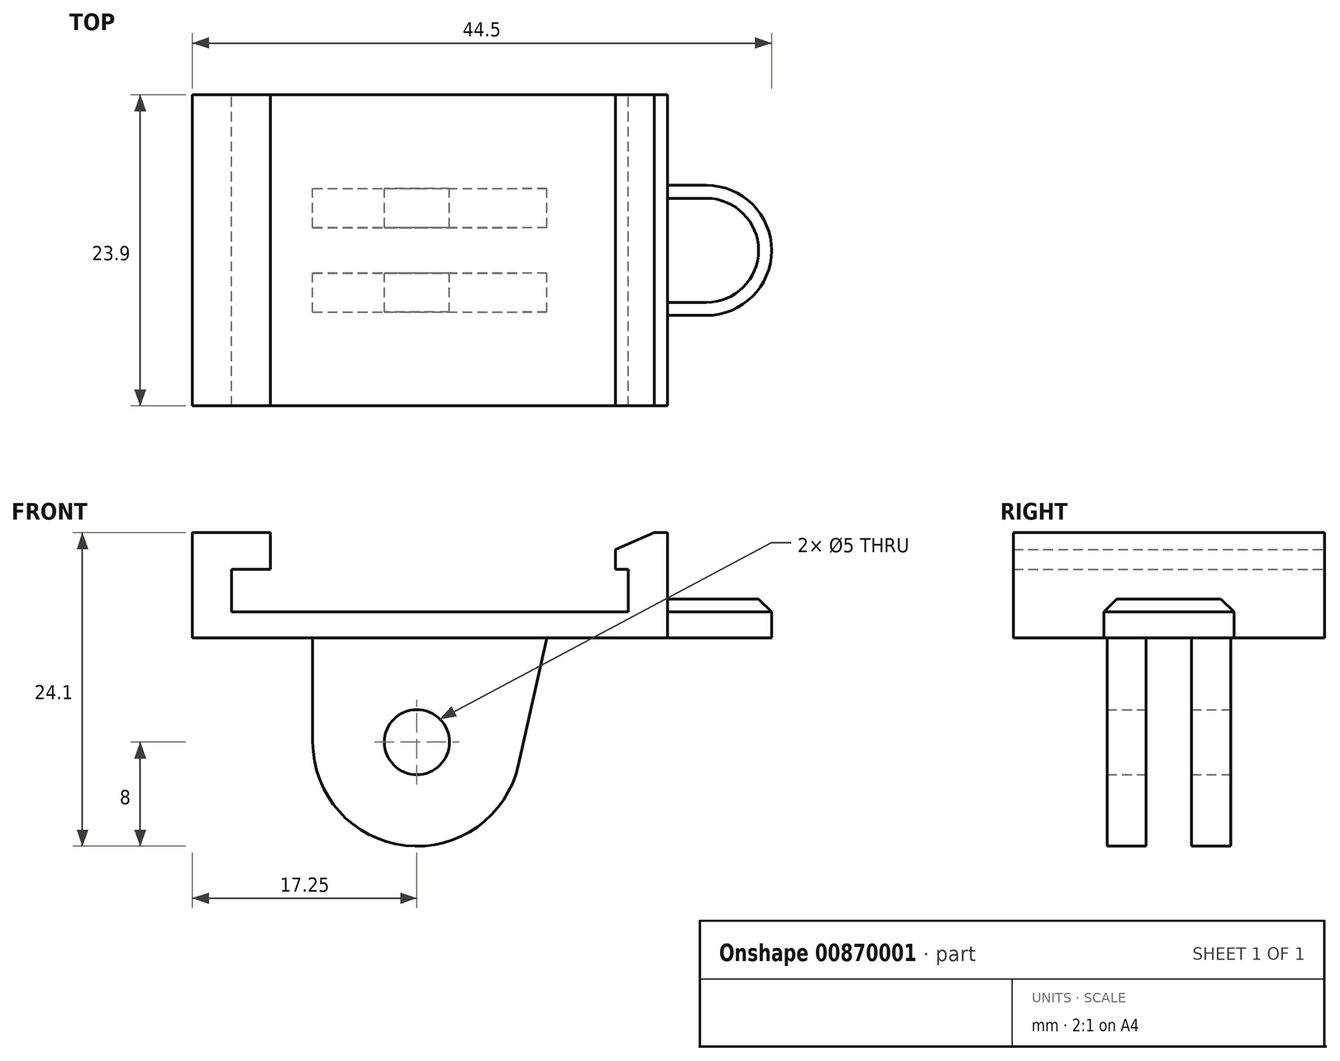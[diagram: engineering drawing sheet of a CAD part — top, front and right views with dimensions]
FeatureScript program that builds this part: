
annotation { "Feature Type Name" : "Feature", "Feature Type Description" : "" }
export const myFeature = defineFeature(function(context is Context, id is Id, definition is map)
    precondition{}
    {
        {
            var Q0;
            Q0=qCreatedBy(makeId("Front.planeOp"),FACE);
            var sketch = newSketch(context, id + "F0", { "sketchPlane" : qUnion([Q0])});
            skLineSegment(sketch, "E0", {"start": v(-12.25, 1.65) * mm, "end": v(-12.25, 4.45) * mm});
            skLineSegment(sketch, "E1", {"start": v(-12.25, 4.45) * mm, "end": v(-18.25, 4.45) * mm});
            skLineSegment(sketch, "E2", {"start": v(-18.25, 4.45) * mm, "end": v(-18.25, -3.65) * mm});
            skLineSegment(sketch, "E3", {"start": v(-18.25, -3.65) * mm, "end": v(18.25, -3.65) * mm});
            skLineSegment(sketch, "E4", {"start": v(18.25, -3.65) * mm, "end": v(18.25, 4.45) * mm});
            skLineSegment(sketch, "E5", {"start": v(14.25, 3.15) * mm, "end": v(14.25, 1.65) * mm});
            skLineSegment(sketch, "E6", {"start": v(15.25, 1.65) * mm, "end": v(15.25, -1.65) * mm});
            skLineSegment(sketch, "E7", {"start": v(15.25, -1.65) * mm, "end": v(-15.25, -1.65) * mm});
            skLineSegment(sketch, "E8", {"start": v(-15.25, -1.65) * mm, "end": v(-15.25, 1.65) * mm});
            skLineSegment(sketch, "E9", {"start": v(-15.25, 1.65) * mm, "end": v(-12.25, 1.65) * mm});
            skLineSegment(sketch, "E10", {"start": v(14.25, 1.65) * mm, "end": v(15.25, 1.65) * mm});
            skLineSegment(sketch, "E11", {"start": v(17.25, 4.45) * mm, "end": v(18.25, 4.45) * mm});
            skLineSegment(sketch, "E12", {"start": v(17.25, 4.45) * mm, "end": v(14.25, 3.15) * mm});
            skSolve(sketch);
        }
        {
            var Q0;
            Q0 = qSketchRegion(id + "F0", true);
            extrude(context, id + "F1", {"entities" : qUnion([Q0]), "endBound" : BoundingType.SYMMETRIC, "depth" : 23.9 * mm, "offsetDistance" : 25 * mm});
        }
        {
            var Q0;
            Q0=qCreatedBy(makeId("Front.planeOp"),FACE);
            var sketch = newSketch(context, id + "F2", { "sketchPlane" : qUnion([Q0])});
            skLineSegment(sketch, "E13", {"start": v(-9, -11.65) * mm, "end": v(-9, -3.65) * mm});
            skLineSegment(sketch, "E14", {"start": v(-9, -3.65) * mm, "end": v(9, -3.65) * mm});
            skLineSegment(sketch, "E15", {"start": v(9, -3.65) * mm, "end": v(6.8, -13.4) * mm});
            skArc(sketch, "E16", {"start": v(-9, -11.65) * mm, "mid": v(-1.88, -19.6) * mm, "end": v(6.8, -13.4) * mm});
            skCircle(sketch, "E17", {"center": v(-1, -11.65) * mm, "radius": 2.5 * mm});
            skSolve(sketch);
        }
        {
            var Q0;
            Q0=makeQuery(id+"F2.imprint","IMPRINT",FACE,{"disambiguationData":[TD([[makeQuery(id+"F2.imprint","IMPRINT",EDGE,{"derivedFrom":sQuery(id+"F2.wireOp",EDGE,"E13")}),-1.0]])]});
            extrude(context, id + "F3", {"entities" : qUnion([Q0]), "operationType" : NewBodyOperationType.ADD, "endBound" : BoundingType.SYMMETRIC, "depth" : 9.5 * mm, "offsetDistance" : 25 * mm});
        }
        {
            var Q0;
            Q0=qCreatedBy(makeId("Right.planeOp"),FACE);
            var sketch = newSketch(context, id + "F4", { "sketchPlane" : qUnion([Q0])});
            skLineSegment(sketch, "E18.bottom", {"start": v(1.75, -25.65) * mm, "end": v(-1.75, -25.65) * mm});
            skLineSegment(sketch, "E18.top", {"start": v(1.75, -3.65) * mm, "end": v(-1.75, -3.65) * mm});
            skLineSegment(sketch, "E18.left", {"start": v(1.75, -25.65) * mm, "end": v(1.75, -3.65) * mm});
            skLineSegment(sketch, "E18.right", {"start": v(-1.75, -25.65) * mm, "end": v(-1.75, -3.65) * mm});
            skSolve(sketch);
        }
        {
            var Q0;
            Q0 = qSketchRegion(id + "F4", true);
            extrude(context, id + "F5", {"entities" : qUnion([Q0]), "operationType" : NewBodyOperationType.REMOVE, "endBound" : BoundingType.SYMMETRIC, "depth" : 25 * mm, "offsetDistance" : 25 * mm});
        }
        {
            var Q0;
            Q0=makeQuery(id+"F5.boolean.opBoolean","MERGE",FACE,{"derivedFrom":[makeQuery(id+"F1.opExtrude","SWEPT_FACE",FACE,{"disambiguationData":[OSD([sQuery(id+"F0.wireOp",EDGE,"E3")])]}),makeQuery(id+"F5.opExtrude","SWEPT_FACE",FACE,{"disambiguationData":[OSD([sQuery(id+"F4.wireOp",EDGE,"E18.top")])]})]});
            var sketch = newSketch(context, id + "F6", { "sketchPlane" : qUnion([Q0])});
            skLineSegment(sketch, "E19.bottom", {"start": v(18.25, -5) * mm, "end": v(21.25, -5) * mm});
            skLineSegment(sketch, "E19.top", {"start": v(18.25, 5) * mm, "end": v(21.25, 5) * mm});
            skLineSegment(sketch, "E19.left", {"start": v(18.25, -5) * mm, "end": v(18.25, 5) * mm});
            skLineSegment(sketch, "E19.right", {"start": v(21.25, -5) * mm, "end": v(21.25, 5) * mm});
            skArc(sketch, "E20", {"start": v(21.25, -5) * mm, "mid": v(26.25, 0) * mm, "end": v(21.25, 5) * mm});
            skSolve(sketch);
        }
        {
            var Q0;
            Q0 = qSketchRegion(id + "F6", true);
            extrude(context, id + "F7", {"entities" : qUnion([Q0]), "operationType" : NewBodyOperationType.ADD, "oppositeDirection" : true, "depth" : 3 * mm, "offsetDistance" : 25 * mm});
        }
        {
            var Q0;
            Q0=makeQuery(id+"F7.opExtrude","CAP_EDGE",EDGE,{"disambiguationData":[OSD([sQuery(id+"F6.wireOp",EDGE,"E20")])],"isStart":false});
            chamfer(context, id + "F8", {"entities" : qUnion([Q0]), "width" : 1 * mm, "tangentPropagation" : true});
        }
    });
